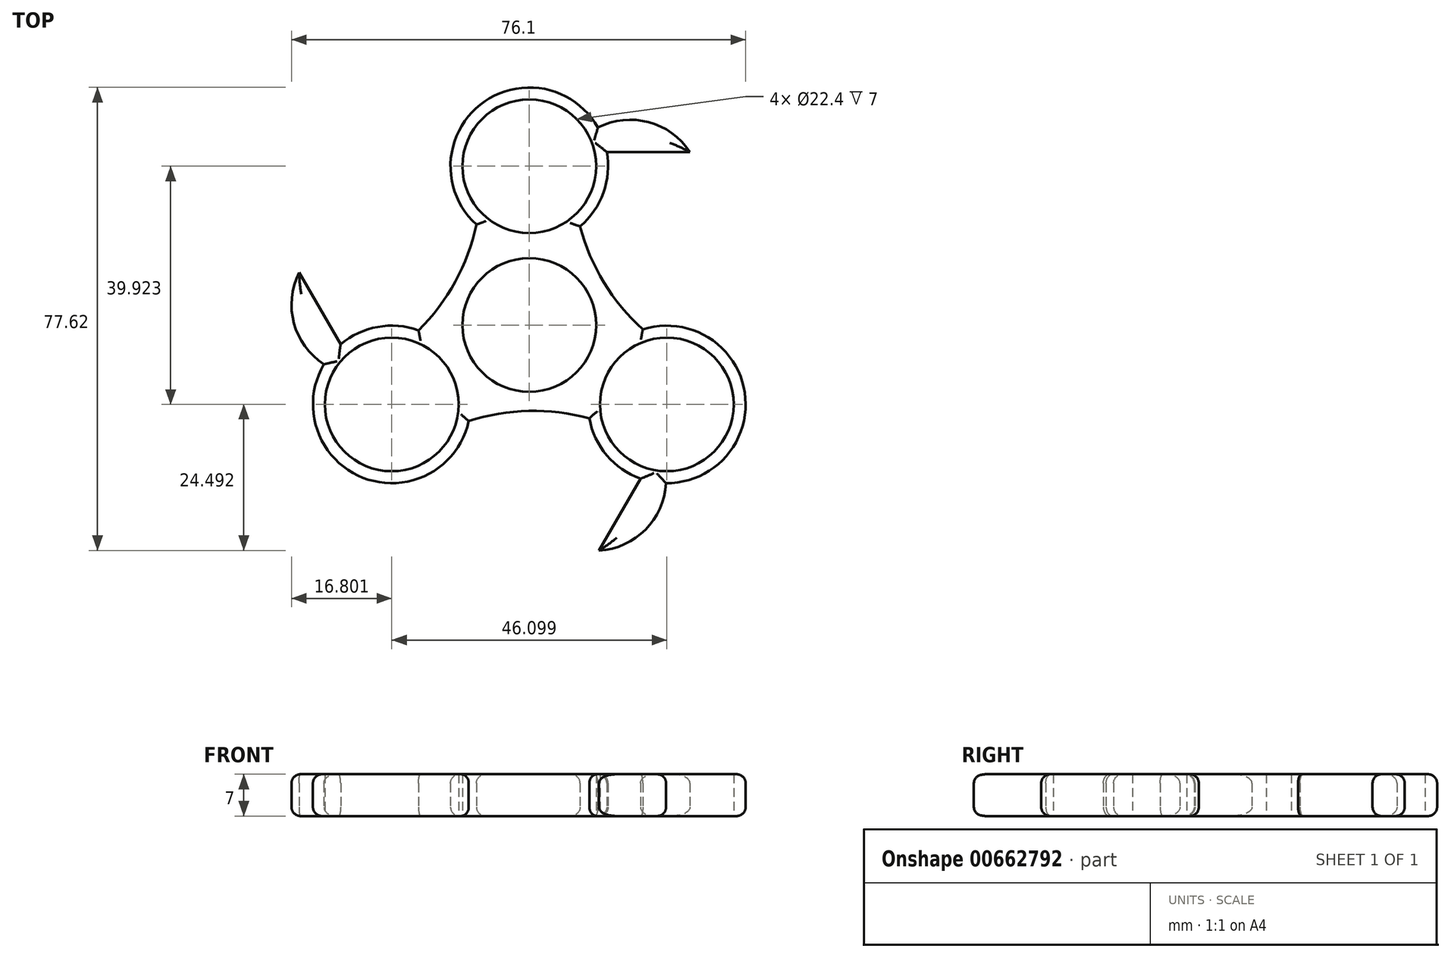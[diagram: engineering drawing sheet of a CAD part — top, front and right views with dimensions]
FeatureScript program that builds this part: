
annotation { "Feature Type Name" : "Feature", "Feature Type Description" : "" }
export const myFeature = defineFeature(function(context is Context, id is Id, definition is map)
    precondition{}
    {
        {
            var Q0;
            Q0=qCreatedBy(makeId("Top.planeOp"),FACE);
            var sketch = newSketch(context, id + "F0", { "sketchPlane" : qUnion([Q0])});
            skCircle(sketch, "E0", {"center": v(0, 0) * mm, "radius": 11.2 * mm});
            skCircle(sketch, "E1", {"center": v(0, 26.62) * mm, "radius": 11.2 * mm});
            skArc(sketch, "E2", {"start": v(8.52, 16.53) * mm, "mid": v(0.24, 39.81) * mm, "end": v(-8.87, 16.84) * mm});
            skArc(sketch, "E3.1.0", {"start": v(-18.58, -0.89) * mm, "mid": v(-34.6, -19.7) * mm, "end": v(-10.15, -16.1) * mm});
            skCircle(sketch, "E3.1.1", {"center": v(-23.05, -13.3) * mm, "radius": 11.2 * mm});
            skArc(sketch, "E3.2.0", {"start": v(10.06, -15.64) * mm, "mid": v(34.36, -20.11) * mm, "end": v(19.02, -0.74) * mm});
            skCircle(sketch, "E3.2.1", {"center": v(23.05, -13.3) * mm, "radius": 11.2 * mm});
            skArc(sketch, "E4", {"start": v(8.52, 16.53) * mm, "mid": v(12.5, 7.13) * mm, "end": v(19.02, -0.74) * mm});
            skArc(sketch, "E5.1.0", {"start": v(-18.58, -0.89) * mm, "mid": v(-12.42, 7.27) * mm, "end": v(-8.87, 16.84) * mm});
            skArc(sketch, "E5.2.0", {"start": v(10.06, -15.64) * mm, "mid": v(-0.08, -14.4) * mm, "end": v(-10.15, -16.1) * mm});
            skArc(sketch, "E6", {"start": v(26.9, 29) * mm, "mid": v(19.98, 34) * mm, "end": v(11.5, 33.1) * mm});
            skLineSegment(sketch, "E7", {"start": v(26.9, 29) * mm, "end": v(12.98, 29) * mm});
            skArc(sketch, "E8.1.0", {"start": v(-38.57, 8.8) * mm, "mid": v(-39.43, 0.3) * mm, "end": v(-34.41, -6.59) * mm});
            skLineSegment(sketch, "E8.1.1", {"start": v(-38.57, 8.8) * mm, "end": v(-31.61, -3.26) * mm});
            skArc(sketch, "E8.2.0", {"start": v(11.67, -37.8) * mm, "mid": v(19.45, -34.3) * mm, "end": v(22.91, -26.5) * mm});
            skLineSegment(sketch, "E8.2.1", {"start": v(11.67, -37.8) * mm, "end": v(18.63, -25.75) * mm});
            skSolve(sketch);
        }
        {
            var Q0;
            Q0=makeQuery(id+"F0.imprint","IMPRINT",FACE,{"disambiguationData":[TD([[makeQuery(id+"F0.imprint","IMPRINT",EDGE,{"derivedFrom":sQuery(id+"F0.wireOp",EDGE,"E0")}),-1.0]])]});
            var Q1;
            {var subQ0=sQuery(id+"F0.wireOp",EDGE,"E8.2.0");Q1=makeQuery(id+"F0.imprint","IMPRINT",FACE,{"disambiguationData":[TD([[makeQuery(id+"F0.imprint","IMPRINT",EDGE,{"derivedFrom":subQ0}),1.0]])]});}
            var Q2;
            {var subQ0=sQuery(id+"F0.wireOp",EDGE,"E8.1.0");Q2=makeQuery(id+"F0.imprint","IMPRINT",FACE,{"disambiguationData":[TD([[makeQuery(id+"F0.imprint","IMPRINT",EDGE,{"derivedFrom":subQ0}),1.0]])]});}
            var Q3;
            {var subQ0=sQuery(id+"F0.wireOp",EDGE,"E6");Q3=makeQuery(id+"F0.imprint","IMPRINT",FACE,{"disambiguationData":[TD([[makeQuery(id+"F0.imprint","IMPRINT",EDGE,{"derivedFrom":subQ0}),1.0]])]});}
            extrude(context, id + "F1", {"entities" : qUnion([Q0, Q1, Q2, Q3]), "depth" : 7 * mm, "offsetDistance" : 25 * mm});
        }
        {
            var Q0;
            Q0=makeQuery(id+"F1.opExtrude","CAP_EDGE",EDGE,{"disambiguationData":[OSD([sQuery(id+"F0.wireOp",EDGE,"E5.2.0")])],"isStart":false});
            var Q1;
            {var subQ0=sQuery(id+"F0.wireOp",EDGE,"E3.1.0");Q1=makeQuery(id+"F1.opExtrude","CAP_EDGE",EDGE,{"disambiguationData":[OSD([subQ0]),TDD([makeQuery(id+"F0.imprint","IMPRINT",EDGE,{"disambiguationData":[TD([[makeQuery(id+"F0.imprint","INTERSECT",VERTEX,{"derivedFrom":[subQ0,sQuery(id+"F0.wireOp",EDGE,"E5.2.0")]}),1.0]])],"derivedFrom":subQ0})])],"isStart":false});}
            var Q2;
            Q2=makeQuery(id+"F1.opExtrude","CAP_EDGE",EDGE,{"disambiguationData":[OSD([sQuery(id+"F0.wireOp",EDGE,"E8.1.0")])],"isStart":false});
            var Q3;
            {var subQ0=sQuery(id+"F0.wireOp",EDGE,"E3.1.0");Q3=makeQuery(id+"F1.opExtrude","CAP_EDGE",EDGE,{"disambiguationData":[OSD([subQ0]),TDD([makeQuery(id+"F0.imprint","IMPRINT",EDGE,{"disambiguationData":[TD([[makeQuery(id+"F0.imprint","INTERSECT",VERTEX,{"derivedFrom":[subQ0,sQuery(id+"F0.wireOp",EDGE,"E5.1.0")]}),-1.0]])],"derivedFrom":subQ0})])],"isStart":false});}
            var Q4;
            Q4=makeQuery(id+"F1.opExtrude","CAP_EDGE",EDGE,{"disambiguationData":[OSD([sQuery(id+"F0.wireOp",EDGE,"E8.1.1")])],"isStart":false});
            var Q5;
            Q5=makeQuery(id+"F1.opExtrude","CAP_EDGE",EDGE,{"disambiguationData":[OSD([sQuery(id+"F0.wireOp",EDGE,"E5.1.0")])],"isStart":false});
            var Q6;
            {var subQ0=sQuery(id+"F0.wireOp",EDGE,"E2");Q6=makeQuery(id+"F1.opExtrude","CAP_EDGE",EDGE,{"disambiguationData":[OSD([subQ0]),TDD([makeQuery(id+"F0.imprint","IMPRINT",EDGE,{"disambiguationData":[TD([[makeQuery(id+"F0.imprint","INTERSECT",VERTEX,{"derivedFrom":[subQ0,sQuery(id+"F0.wireOp",EDGE,"E5.1.0")]}),1.0]])],"derivedFrom":subQ0})])],"isStart":false});}
            var Q7;
            Q7=makeQuery(id+"F1.opExtrude","CAP_EDGE",EDGE,{"disambiguationData":[OSD([sQuery(id+"F0.wireOp",EDGE,"E6")])],"isStart":false});
            var Q8;
            {var subQ0=sQuery(id+"F0.wireOp",EDGE,"E2");Q8=makeQuery(id+"F1.opExtrude","CAP_EDGE",EDGE,{"disambiguationData":[OSD([subQ0]),TDD([makeQuery(id+"F0.imprint","IMPRINT",EDGE,{"disambiguationData":[TD([[makeQuery(id+"F0.imprint","INTERSECT",VERTEX,{"derivedFrom":[subQ0,sQuery(id+"F0.wireOp",EDGE,"E4")]}),-1.0]])],"derivedFrom":subQ0})])],"isStart":false});}
            var Q9;
            Q9=makeQuery(id+"F1.opExtrude","CAP_EDGE",EDGE,{"disambiguationData":[OSD([sQuery(id+"F0.wireOp",EDGE,"E7")])],"isStart":false});
            var Q10;
            Q10=makeQuery(id+"F1.opExtrude","CAP_EDGE",EDGE,{"disambiguationData":[OSD([sQuery(id+"F0.wireOp",EDGE,"E4")])],"isStart":false});
            var Q11;
            {var subQ0=sQuery(id+"F0.wireOp",EDGE,"E3.2.0");Q11=makeQuery(id+"F1.opExtrude","CAP_EDGE",EDGE,{"disambiguationData":[OSD([subQ0]),TDD([makeQuery(id+"F0.imprint","IMPRINT",EDGE,{"disambiguationData":[TD([[makeQuery(id+"F0.imprint","INTERSECT",VERTEX,{"derivedFrom":[subQ0,sQuery(id+"F0.wireOp",EDGE,"E4")]}),1.0]])],"derivedFrom":subQ0})])],"isStart":false});}
            var Q12;
            Q12=makeQuery(id+"F1.opExtrude","CAP_EDGE",EDGE,{"disambiguationData":[OSD([sQuery(id+"F0.wireOp",EDGE,"E8.2.0")])],"isStart":false});
            var Q13;
            {var subQ0=sQuery(id+"F0.wireOp",EDGE,"E3.2.0");Q13=makeQuery(id+"F1.opExtrude","CAP_EDGE",EDGE,{"disambiguationData":[OSD([subQ0]),TDD([makeQuery(id+"F0.imprint","IMPRINT",EDGE,{"disambiguationData":[TD([[makeQuery(id+"F0.imprint","INTERSECT",VERTEX,{"derivedFrom":[subQ0,sQuery(id+"F0.wireOp",EDGE,"E5.2.0")]}),-1.0]])],"derivedFrom":subQ0})])],"isStart":false});}
            var Q14;
            Q14=makeQuery(id+"F1.opExtrude","CAP_EDGE",EDGE,{"disambiguationData":[OSD([sQuery(id+"F0.wireOp",EDGE,"E8.2.1")])],"isStart":false});
            var Q15;
            {var subQ0=sQuery(id+"F0.wireOp",EDGE,"E2");Q15=makeQuery(id+"F1.opExtrude","CAP_EDGE",EDGE,{"disambiguationData":[OSD([subQ0]),TDD([makeQuery(id+"F0.imprint","IMPRINT",EDGE,{"disambiguationData":[TD([[makeQuery(id+"F0.imprint","INTERSECT",VERTEX,{"derivedFrom":[subQ0,sQuery(id+"F0.wireOp",EDGE,"E5.1.0")]}),1.0]])],"derivedFrom":subQ0})])],"isStart":true});}
            var Q16;
            Q16=makeQuery(id+"F1.opExtrude","CAP_EDGE",EDGE,{"disambiguationData":[OSD([sQuery(id+"F0.wireOp",EDGE,"E6")])],"isStart":true});
            var Q17;
            Q17=makeQuery(id+"F1.opExtrude","CAP_EDGE",EDGE,{"disambiguationData":[OSD([sQuery(id+"F0.wireOp",EDGE,"E7")])],"isStart":true});
            var Q18;
            {var subQ0=sQuery(id+"F0.wireOp",EDGE,"E2");Q18=makeQuery(id+"F1.opExtrude","CAP_EDGE",EDGE,{"disambiguationData":[OSD([subQ0]),TDD([makeQuery(id+"F0.imprint","IMPRINT",EDGE,{"disambiguationData":[TD([[makeQuery(id+"F0.imprint","INTERSECT",VERTEX,{"derivedFrom":[subQ0,sQuery(id+"F0.wireOp",EDGE,"E4")]}),-1.0]])],"derivedFrom":subQ0})])],"isStart":true});}
            var Q19;
            Q19=makeQuery(id+"F1.opExtrude","CAP_EDGE",EDGE,{"disambiguationData":[OSD([sQuery(id+"F0.wireOp",EDGE,"E4")])],"isStart":true});
            var Q20;
            {var subQ0=sQuery(id+"F0.wireOp",EDGE,"E3.2.0");Q20=makeQuery(id+"F1.opExtrude","CAP_EDGE",EDGE,{"disambiguationData":[OSD([subQ0]),TDD([makeQuery(id+"F0.imprint","IMPRINT",EDGE,{"disambiguationData":[TD([[makeQuery(id+"F0.imprint","INTERSECT",VERTEX,{"derivedFrom":[subQ0,sQuery(id+"F0.wireOp",EDGE,"E4")]}),1.0]])],"derivedFrom":subQ0})])],"isStart":true});}
            var Q21;
            Q21=makeQuery(id+"F1.opExtrude","CAP_EDGE",EDGE,{"disambiguationData":[OSD([sQuery(id+"F0.wireOp",EDGE,"E8.2.0")])],"isStart":true});
            var Q22;
            {var subQ0=sQuery(id+"F0.wireOp",EDGE,"E3.2.0");Q22=makeQuery(id+"F1.opExtrude","CAP_EDGE",EDGE,{"disambiguationData":[OSD([subQ0]),TDD([makeQuery(id+"F0.imprint","IMPRINT",EDGE,{"disambiguationData":[TD([[makeQuery(id+"F0.imprint","INTERSECT",VERTEX,{"derivedFrom":[subQ0,sQuery(id+"F0.wireOp",EDGE,"E5.2.0")]}),-1.0]])],"derivedFrom":subQ0})])],"isStart":true});}
            var Q23;
            Q23=makeQuery(id+"F1.opExtrude","CAP_EDGE",EDGE,{"disambiguationData":[OSD([sQuery(id+"F0.wireOp",EDGE,"E8.2.1")])],"isStart":true});
            var Q24;
            Q24=makeQuery(id+"F1.opExtrude","CAP_EDGE",EDGE,{"disambiguationData":[OSD([sQuery(id+"F0.wireOp",EDGE,"E5.2.0")])],"isStart":true});
            var Q25;
            {var subQ0=sQuery(id+"F0.wireOp",EDGE,"E3.1.0");Q25=makeQuery(id+"F1.opExtrude","CAP_EDGE",EDGE,{"disambiguationData":[OSD([subQ0]),TDD([makeQuery(id+"F0.imprint","IMPRINT",EDGE,{"disambiguationData":[TD([[makeQuery(id+"F0.imprint","INTERSECT",VERTEX,{"derivedFrom":[subQ0,sQuery(id+"F0.wireOp",EDGE,"E5.2.0")]}),1.0]])],"derivedFrom":subQ0})])],"isStart":true});}
            var Q26;
            Q26=makeQuery(id+"F1.opExtrude","CAP_EDGE",EDGE,{"disambiguationData":[OSD([sQuery(id+"F0.wireOp",EDGE,"E8.1.0")])],"isStart":true});
            var Q27;
            Q27=makeQuery(id+"F1.opExtrude","CAP_EDGE",EDGE,{"disambiguationData":[OSD([sQuery(id+"F0.wireOp",EDGE,"E5.1.0")])],"isStart":true});
            var Q28;
            Q28=makeQuery(id+"F1.opExtrude","CAP_EDGE",EDGE,{"disambiguationData":[OSD([sQuery(id+"F0.wireOp",EDGE,"E8.1.1")])],"isStart":true});
            var Q29;
            {var subQ0=sQuery(id+"F0.wireOp",EDGE,"E3.1.0");Q29=makeQuery(id+"F1.opExtrude","CAP_EDGE",EDGE,{"disambiguationData":[OSD([subQ0]),TDD([makeQuery(id+"F0.imprint","IMPRINT",EDGE,{"disambiguationData":[TD([[makeQuery(id+"F0.imprint","INTERSECT",VERTEX,{"derivedFrom":[subQ0,sQuery(id+"F0.wireOp",EDGE,"E5.1.0")]}),-1.0]])],"derivedFrom":subQ0})])],"isStart":true});}
            fillet(context, id + "F2", {"entities" : qUnion([Q0, Q1, Q2, Q3, Q4, Q5, Q6, Q7, Q8, Q9, Q10, Q11, Q12, Q13, Q14, Q15, Q16, Q17, Q18, Q19, Q20, Q21, Q22, Q23, Q24, Q25, Q26, Q27, Q28, Q29]), "radius" : 1.5 * mm, "tangentPropagation" : true, "allowEdgeOverflow" : false});
        }
    });
